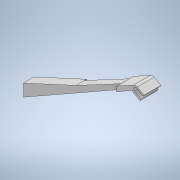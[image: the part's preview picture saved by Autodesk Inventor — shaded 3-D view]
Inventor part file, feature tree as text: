
AUTODESK INVENTOR PART (.ipt)
format: ipt  version: 2020 (Build 240168000, 168)  size: 180,736 bytes
history: native  units: mm
features: extrude x3, sketch x3, mirror x1
ambient origin geometry x8: Origin, YZ Plane, XZ Plane, XY Plane, X Axis, Y Axis, Z Axis, Center Point
bodies: Solid1 (feature_tree)
feature tree (7):
  extrude  "Extrusion1"  Depth=279.931505mm
  extrude  "Extrusion2"  Depth=4.336878mm
  mirror  "Mirror1"
  extrude  "Extrusion3"  Depth=10.0mm
  sketch  "Sketch1"  dims[d7=588.239625mm d8=279.931505mm]
  sketch  "Sketch2"  dims[d9=5.165078mm d10=4.336878mm]
  sketch  "Sketch3"  dims[d11=4.88916mm d12=5.376748mm d13=248.002124mm d14=211.001419mm d15=171.972718mm d16=284.224916mm d17=316.226348mm d18=60.0deg d19=26.17928mm d20=312.190756mm d21=15.707979mm d22=15.707948mm d23=90.0deg d24=21.124696mm d25=17.260897mm d26=12.172251mm d27=10.567205mm d28=12.649124mm d29=9.995658mm d30=18.294689mm d31=80.0mm d32=0.0mm d33=10.330604mm d34=20.0mm d35=0.0mm d36=10.0mm d37=0.0mm]
